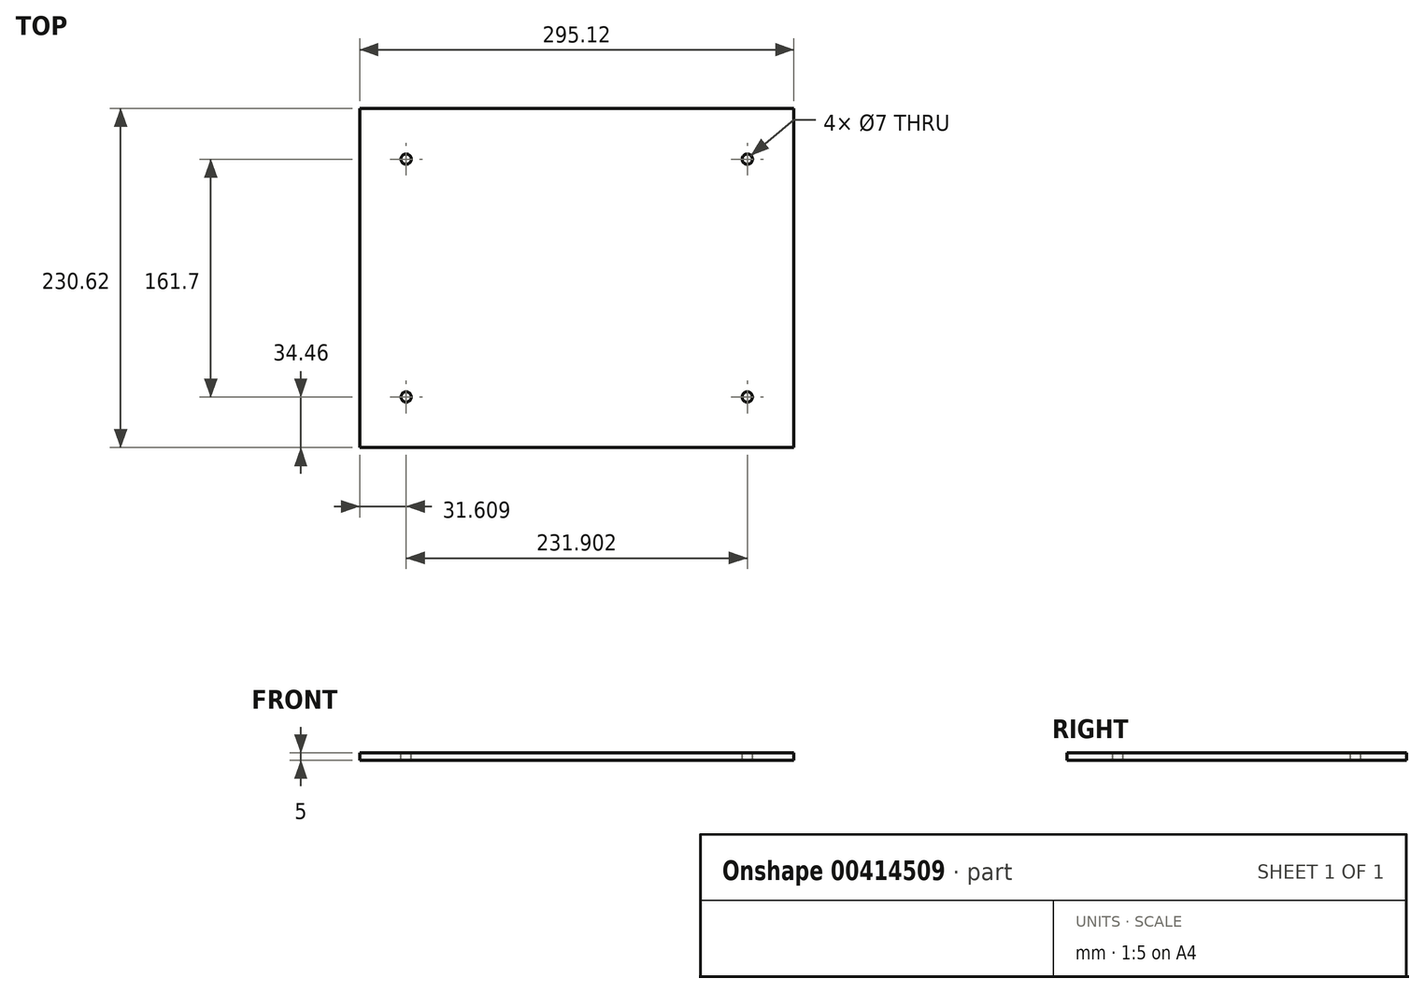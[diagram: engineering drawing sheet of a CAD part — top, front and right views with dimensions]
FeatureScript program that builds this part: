
annotation { "Feature Type Name" : "Feature", "Feature Type Description" : "" }
export const myFeature = defineFeature(function(context is Context, id is Id, definition is map)
    precondition{}
    {
        {
            var Q0;
            Q0=qCreatedBy(makeId("Top.planeOp"),FACE);
            var sketch = newSketch(context, id + "F0", { "sketchPlane" : qUnion([Q0])});
            skLineSegment(sketch, "E0.bottom", {"start": v(-147.56, 115.31) * mm, "end": v(147.56, 115.31) * mm});
            skLineSegment(sketch, "E0.top", {"start": v(-147.56, -115.31) * mm, "end": v(147.56, -115.31) * mm});
            skLineSegment(sketch, "E0.left", {"start": v(-147.56, 115.31) * mm, "end": v(-147.56, -115.31) * mm});
            skLineSegment(sketch, "E0.right", {"start": v(147.56, 115.31) * mm, "end": v(147.56, -115.31) * mm});
            skPoint(sketch, "E0.middle", {"position": v(0, 0) * mm});
            skSolve(sketch);
        }
        {
            var Q0;
            Q0=makeQuery(id+"F0.imprint","IMPRINT",FACE,{"disambiguationData":[TD([[makeQuery(id+"F0.imprint","IMPRINT",EDGE,{"derivedFrom":sQuery(id+"F0.wireOp",EDGE,"E0.bottom")}),-1.0]])]});
            extrude(context, id + "F1", {"entities" : qUnion([Q0]), "depth" : 5 * mm});
        }
        {
            var Q0;
            Q0=makeQuery(id+"F1.opExtrude","CAP_FACE",FACE,{"disambiguationData":[OSD([sQuery(id+"F0.wireOp",EDGE,"E0.bottom"),sQuery(id+"F0.wireOp",EDGE,"E0.top"),sQuery(id+"F0.wireOp",EDGE,"E0.left"),sQuery(id+"F0.wireOp",EDGE,"E0.right")])],"isStart":false});
            var sketch = newSketch(context, id + "F2", { "sketchPlane" : qUnion([Q0])});
            skLineSegment(sketch, "E1.bottom", {"start": v(-115.95, 80.85) * mm, "end": v(115.95, 80.85) * mm, "construction": true});
            skLineSegment(sketch, "E1.top", {"start": v(-115.95, -80.85) * mm, "end": v(115.95, -80.85) * mm, "construction": true});
            skLineSegment(sketch, "E1.left", {"start": v(-115.95, 80.85) * mm, "end": v(-115.95, -80.85) * mm, "construction": true});
            skLineSegment(sketch, "E1.right", {"start": v(115.95, 80.85) * mm, "end": v(115.95, -80.85) * mm, "construction": true});
            skPoint(sketch, "E1.middle", {"position": v(0, 0) * mm});
            skPoint(sketch, "E2", {"position": v(-115.95, 80.85) * mm});
            skPoint(sketch, "E3", {"position": v(115.95, 80.85) * mm});
            skPoint(sketch, "E4", {"position": v(115.95, -80.85) * mm});
            skPoint(sketch, "E5", {"position": v(-115.95, -80.85) * mm});
            skSolve(sketch);
        }
        {
            var Q0;
            Q0=sQuery(id+"F2.wireOp",VERTEX,"E2");
            var Q1;
            Q1=sQuery(id+"F2.wireOp",VERTEX,"E5");
            var Q2;
            Q2=sQuery(id+"F2.wireOp",VERTEX,"E4");
            var Q3;
            Q3=sQuery(id+"F2.wireOp",VERTEX,"E3");
            var Q4;
            Q4=makeQuery(id+"F1.opExtrude","SWEPT_BODY",BODY,{"disambiguationData":[OSD([sQuery(id+"F0.wireOp",EDGE,"E0.bottom"),sQuery(id+"F0.wireOp",EDGE,"E0.top"),sQuery(id+"F0.wireOp",EDGE,"E0.left"),sQuery(id+"F0.wireOp",EDGE,"E0.right")])]});
            hole(context, id + "F3", {"style" : HoleStyle.SIMPLE, "endStyle" : HoleEndStyle.THROUGH, "standardTappedOrClearance" : lookupTablePath({ "standard" : "ISO", "engagement" : "75%", "pitch" : "1 mm", "size" : "M8", "type" : "Tapped" }), "standardBlindInLast" : lookupTablePath({ "standard" : "ISO", "engagement" : "75%", "pitch" : "1 mm", "size" : "M8", "type" : "Tapped" }), "holeDiameter" : 7 * mm, "showTappedDepth" : true, "tappedDepth" : 5 * mm, "tapClearance" : 2, "startFromSketch" : true, "locations" : qUnion([Q0, Q1, Q2, Q3]), "scope" : qUnion([Q4]), "majorDiameter" : 8 * mm});
        }
    });
